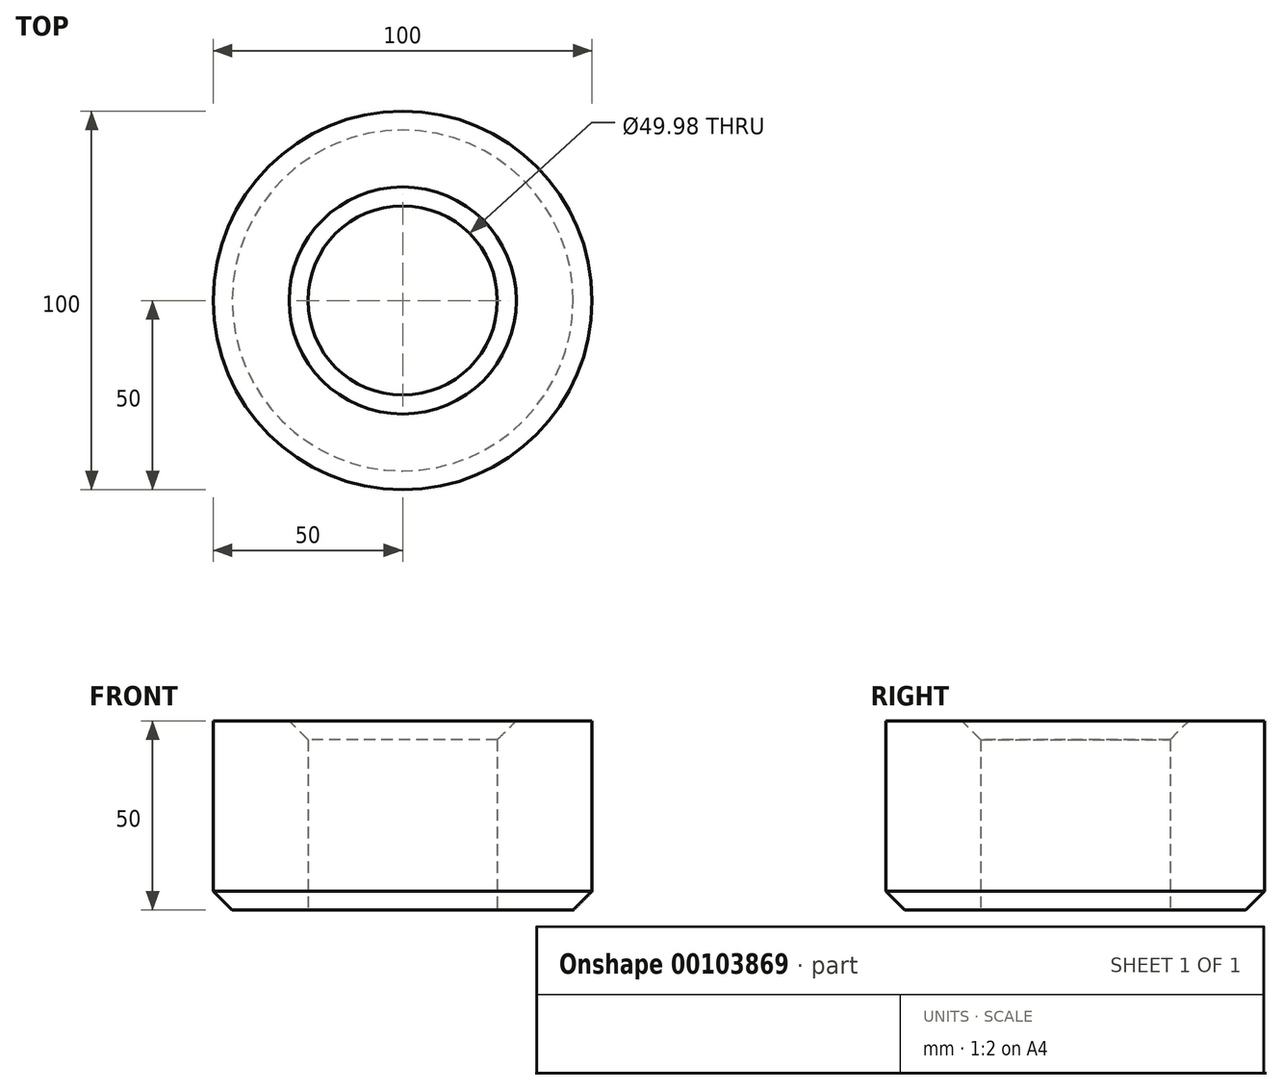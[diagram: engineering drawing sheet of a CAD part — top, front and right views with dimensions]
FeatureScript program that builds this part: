
annotation { "Feature Type Name" : "Feature", "Feature Type Description" : "" }
export const myFeature = defineFeature(function(context is Context, id is Id, definition is map)
    precondition{}
    {
        {
            var Q0;
            Q0=qCreatedBy(makeId("Top.planeOp"),FACE);
            var sketch = newSketch(context, id + "F0", { "sketchPlane" : qUnion([Q0])});
            skCircle(sketch, "E0", {"center": v(0, 0) * mm, "radius": 24.99 * mm});
            skCircle(sketch, "E1", {"center": v(0, 0) * mm, "radius": 50 * mm});
            skSolve(sketch);
        }
        {
            var Q0;
            Q0=makeQuery(id+"F0.imprint","IMPRINT",FACE,{"disambiguationData":[TD([[makeQuery(id+"F0.imprint","IMPRINT",EDGE,{"derivedFrom":sQuery(id+"F0.wireOp",EDGE,"E0")}),-1.0]])]});
            extrude(context, id + "F1", {"entities" : qUnion([Q0]), "depth" : 50 * mm});
        }
        {
            var Q0;
            Q0=makeQuery(id+"F1.opExtrude","CAP_EDGE",EDGE,{"disambiguationData":[OSD([sQuery(id+"F0.wireOp",EDGE,"E0")])],"isStart":false});
            chamfer(context, id + "F2", {"entities" : qUnion([Q0]), "width" : 5 * mm, "tangentPropagation" : true});
        }
        {
            var Q0;
            Q0=makeQuery(id+"F1.opExtrude","CAP_EDGE",EDGE,{"disambiguationData":[OSD([sQuery(id+"F0.wireOp",EDGE,"E1")])],"isStart":true});
            chamfer(context, id + "F3", {"entities" : qUnion([Q0]), "width" : 5 * mm, "tangentPropagation" : true});
        }
    });
